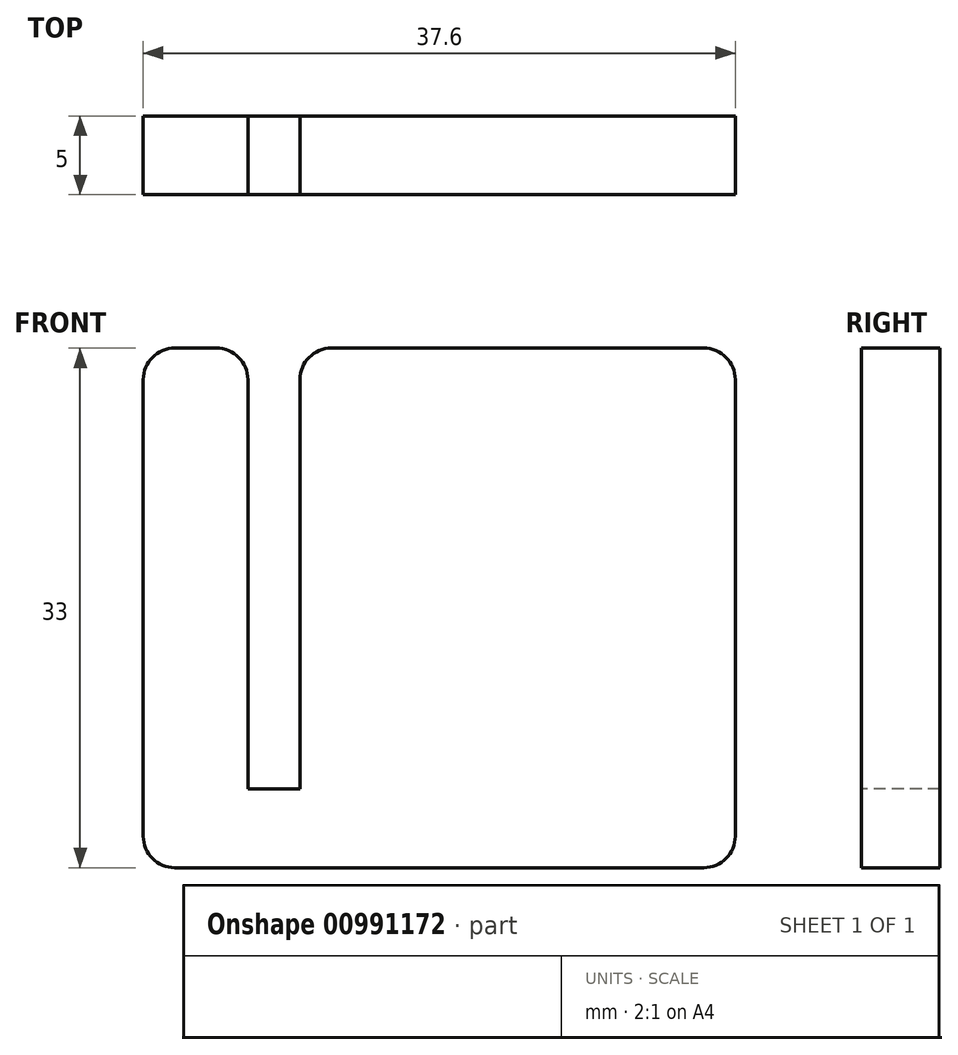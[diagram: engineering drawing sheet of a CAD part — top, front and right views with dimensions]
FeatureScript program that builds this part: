
annotation { "Feature Type Name" : "Feature", "Feature Type Description" : "" }
export const myFeature = defineFeature(function(context is Context, id is Id, definition is map)
    precondition{}
    {
        {
            var Q0;
            Q0=qCreatedBy(makeId("Front.planeOp"),FACE);
            var sketch = newSketch(context, id + "F0", { "sketchPlane" : qUnion([Q0])});
            skLineSegment(sketch, "E0", {"start": v(0, 0) * mm, "end": v(0, -33) * mm});
            skLineSegment(sketch, "E1", {"start": v(0, -33) * mm, "end": v(-37.6, -33) * mm});
            skLineSegment(sketch, "E2", {"start": v(-37.6, -33) * mm, "end": v(-37.6, 0) * mm});
            skLineSegment(sketch, "E3", {"start": v(-37.6, 0) * mm, "end": v(-30.95, 0) * mm});
            skLineSegment(sketch, "E4", {"start": v(-30.95, 0) * mm, "end": v(-30.95, -28) * mm});
            skLineSegment(sketch, "E5", {"start": v(-30.95, -28) * mm, "end": v(-27.65, -28) * mm});
            skLineSegment(sketch, "E6", {"start": v(-27.65, -28) * mm, "end": v(-27.65, 0) * mm});
            skLineSegment(sketch, "E7", {"start": v(-27.65, 0) * mm, "end": v(0, 0) * mm});
            skSolve(sketch);
        }
        {
            var Q0;
            Q0=makeQuery(id+"F0.imprint","IMPRINT",FACE,{"disambiguationData":[TD([[makeQuery(id+"F0.imprint","IMPRINT",EDGE,{"derivedFrom":sQuery(id+"F0.wireOp",EDGE,"E0")}),-1.0]])]});
            extrude(context, id + "F1", {"entities" : qUnion([Q0]), "oppositeDirection" : true, "depth" : 5 * mm, "offsetDistance" : 25 * mm});
        }
        {
            var Q0;
            Q0=makeQuery(id+"F1.opExtrude","SWEPT_EDGE",EDGE,{"disambiguationData":[OSD([sQuery(id+"F0.wireOp",EDGE,"E2"),sQuery(id+"F0.wireOp",EDGE,"E3")])]});
            var Q1;
            Q1=makeQuery(id+"F1.opExtrude","SWEPT_EDGE",EDGE,{"disambiguationData":[OSD([sQuery(id+"F0.wireOp",EDGE,"E3"),sQuery(id+"F0.wireOp",EDGE,"E4")])]});
            var Q2;
            Q2=makeQuery(id+"F1.opExtrude","SWEPT_EDGE",EDGE,{"disambiguationData":[OSD([sQuery(id+"F0.wireOp",EDGE,"E6"),sQuery(id+"F0.wireOp",EDGE,"E7")])]});
            var Q3;
            Q3=makeQuery(id+"F1.opExtrude","SWEPT_EDGE",EDGE,{"disambiguationData":[OSD([sQuery(id+"F0.wireOp",EDGE,"E0"),sQuery(id+"F0.wireOp",EDGE,"E7")])]});
            var Q4;
            Q4=makeQuery(id+"F1.opExtrude","SWEPT_EDGE",EDGE,{"disambiguationData":[OSD([sQuery(id+"F0.wireOp",EDGE,"E0"),sQuery(id+"F0.wireOp",EDGE,"E1")])]});
            var Q5;
            Q5=makeQuery(id+"F1.opExtrude","SWEPT_EDGE",EDGE,{"disambiguationData":[OSD([sQuery(id+"F0.wireOp",EDGE,"E1"),sQuery(id+"F0.wireOp",EDGE,"E2")])]});
            fillet(context, id + "F2", {"entities" : qUnion([Q0, Q1, Q2, Q3, Q4, Q5]), "radius" : 2 * mm, "tangentPropagation" : true, "allowEdgeOverflow" : false});
        }
    });
